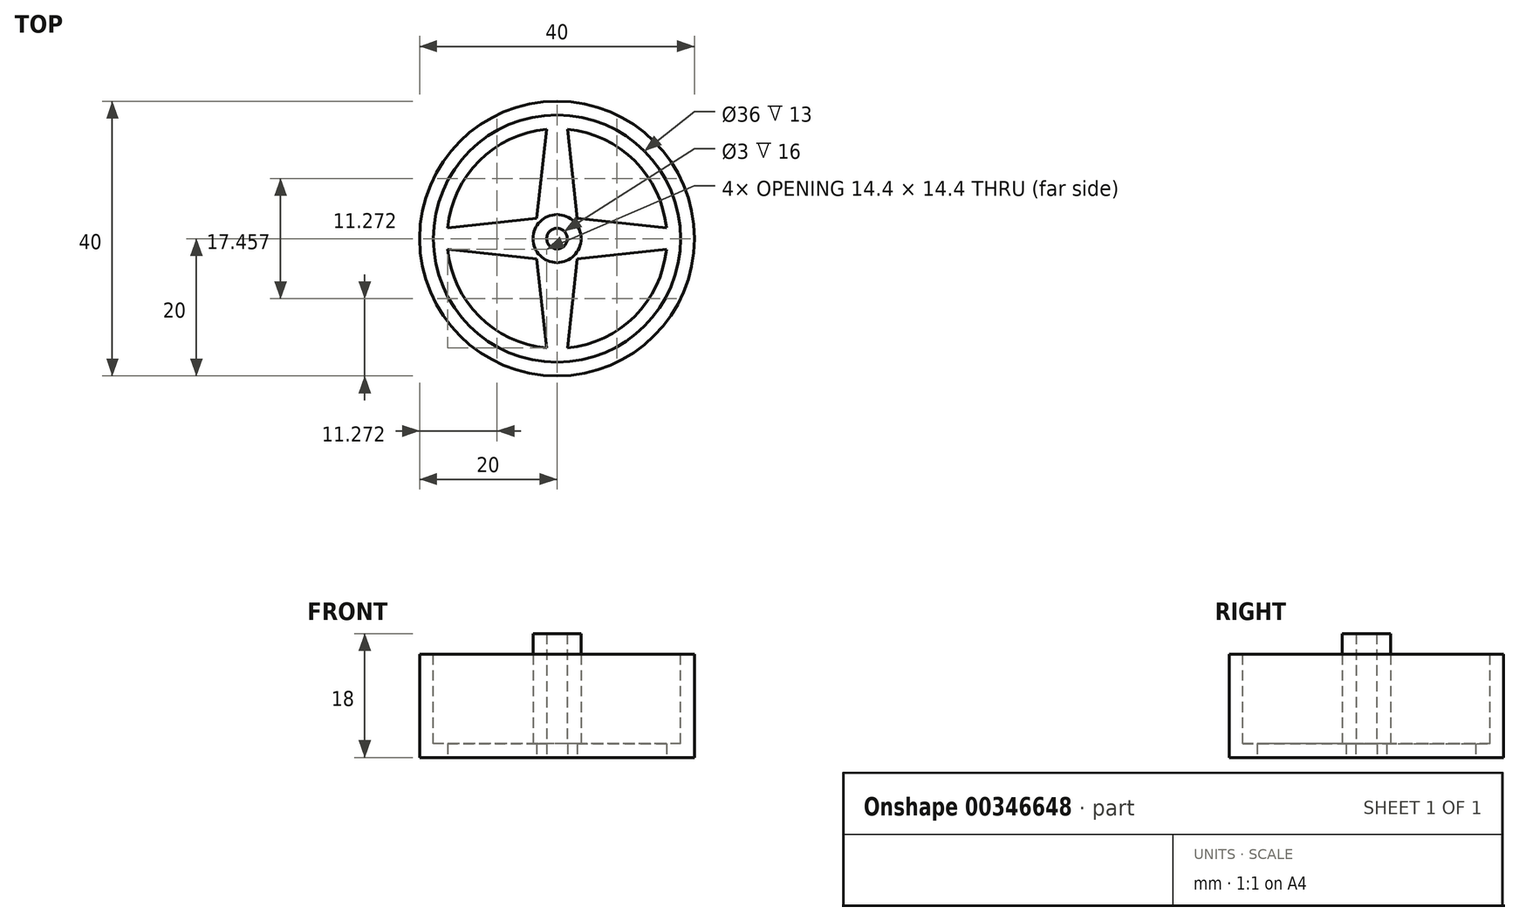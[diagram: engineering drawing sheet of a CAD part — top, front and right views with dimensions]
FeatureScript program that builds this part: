
annotation { "Feature Type Name" : "Feature", "Feature Type Description" : "" }
export const myFeature = defineFeature(function(context is Context, id is Id, definition is map)
    precondition{}
    {
        {
            var Q0;
            Q0=qCreatedBy(makeId("Top.planeOp"),FACE);
            var sketch = newSketch(context, id + "F0", { "sketchPlane" : qUnion([Q0])});
            skCircle(sketch, "E0", {"center": v(0, 0) * mm, "radius": 20 * mm});
            skSolve(sketch);
        }
        {
            var Q0;
            Q0=makeQuery(id+"F0.imprint","IMPRINT",FACE,{"disambiguationData":[TD([[makeQuery(id+"F0.imprint","IMPRINT",EDGE,{"derivedFrom":sQuery(id+"F0.wireOp",EDGE,"E0")}),1.0]])]});
            extrude(context, id + "F1", {"entities" : qUnion([Q0]), "depth" : 15 * mm});
        }
        {
            var Q0;
            Q0=makeQuery(id+"F1.opExtrude","CAP_FACE",FACE,{"disambiguationData":[OSD([sQuery(id+"F0.wireOp",EDGE,"E0")])],"isStart":false});
            var sketch = newSketch(context, id + "F2", { "sketchPlane" : qUnion([Q0])});
            skCircle(sketch, "E1", {"center": v(0, 0) * mm, "radius": 18 * mm});
            skSolve(sketch);
        }
        {
            var Q0;
            Q0=makeQuery(id+"F2.imprint","IMPRINT",FACE,{"disambiguationData":[TD([[makeQuery(id+"F2.imprint","IMPRINT",EDGE,{"derivedFrom":sQuery(id+"F2.wireOp",EDGE,"E1")}),1.0]])]});
            extrude(context, id + "F3", {"entities" : qUnion([Q0]), "operationType" : NewBodyOperationType.REMOVE, "oppositeDirection" : true, "depth" : 13 * mm});
        }
        {
            var Q0;
            Q0=makeQuery(id+"F3.boolean.opBoolean","COPY",FACE,{"derivedFrom":makeQuery(id+"F3.opExtrude","CAP_FACE",FACE,{"disambiguationData":[OSD([sQuery(id+"F2.wireOp",EDGE,"E1")])],"isStart":false})});
            var sketch = newSketch(context, id + "F4", { "sketchPlane" : qUnion([Q0])});
            skCircle(sketch, "E2", {"center": v(0, 0) * mm, "radius": 1.5 * mm});
            skCircle(sketch, "E3", {"center": v(0, 0) * mm, "radius": 3.5 * mm});
            skSolve(sketch);
        }
        {
            var Q0;
            Q0=makeQuery(id+"F4.imprint","IMPRINT",FACE,{"disambiguationData":[TD([[makeQuery(id+"F4.imprint","IMPRINT",EDGE,{"derivedFrom":sQuery(id+"F4.wireOp",EDGE,"E2")}),-1.0]])]});
            extrude(context, id + "F5", {"entities" : qUnion([Q0]), "operationType" : NewBodyOperationType.ADD, "depth" : 16 * mm});
        }
        {
            var Q0;
            Q0=makeQuery(id+"F1.opExtrude","CAP_FACE",FACE,{"disambiguationData":[OSD([sQuery(id+"F0.wireOp",EDGE,"E0")])],"isStart":true});
            var sketch = newSketch(context, id + "F6", { "sketchPlane" : qUnion([Q0])});
            skCircle(sketch, "E4", {"center": v(0, 0) * mm, "radius": 18 * mm});
            skCircle(sketch, "E5", {"center": v(0, 0) * mm, "radius": 3.5 * mm});
            skCircle(sketch, "E6", {"center": v(0, 0) * mm, "radius": 16 * mm});
            skPoint(sketch, "E7.orphan", {"position": v(0, 18) * mm});
            skLineSegment(sketch, "E8", {"start": v(-3.09, 1.65) * mm, "end": v(-1.53, 15.93) * mm});
            skLineSegment(sketch, "E9.MirrorCS", {"start": v(3.09, 1.65) * mm, "end": v(1.53, 15.93) * mm});
            skLineSegment(sketch, "E10.1.0", {"start": v(-1.65, 3.09) * mm, "end": v(-15.93, 1.53) * mm});
            skLineSegment(sketch, "E10.1.1", {"start": v(-1.65, -3.09) * mm, "end": v(-15.93, -1.53) * mm});
            skLineSegment(sketch, "E10.2.0", {"start": v(-3.09, -1.65) * mm, "end": v(-1.53, -15.93) * mm});
            skLineSegment(sketch, "E10.2.1", {"start": v(3.09, -1.65) * mm, "end": v(1.53, -15.93) * mm});
            skLineSegment(sketch, "E10.3.0", {"start": v(1.65, -3.09) * mm, "end": v(15.93, -1.53) * mm});
            skLineSegment(sketch, "E10.3.1", {"start": v(1.65, 3.09) * mm, "end": v(15.93, 1.53) * mm});
            skSolve(sketch);
        }
        {
            var Q0;
            {var subQ0=sQuery(id+"F6.wireOp",EDGE,"E8");var subQ1=sQuery(id+"F6.wireOp",EDGE,"E6");var subQ2=makeQuery(id+"F6.imprint","INTERSECT",VERTEX,{"derivedFrom":[subQ1,subQ0]});Q0=makeQuery(id+"F6.imprint","IMPRINT",FACE,{"disambiguationData":[TD([[makeQuery(id+"F6.imprint","IMPRINT",EDGE,{"disambiguationData":[TD([[subQ2,-1.0]])],"derivedFrom":subQ1}),1.0]])]});}
            var Q1;
            {var subQ0=sQuery(id+"F6.wireOp",EDGE,"E10.1.1");var subQ1=sQuery(id+"F6.wireOp",EDGE,"E6");var subQ2=makeQuery(id+"F6.imprint","INTERSECT",VERTEX,{"derivedFrom":[subQ1,subQ0]});Q1=makeQuery(id+"F6.imprint","IMPRINT",FACE,{"disambiguationData":[TD([[makeQuery(id+"F6.imprint","IMPRINT",EDGE,{"disambiguationData":[TD([[subQ2,-1.0]])],"derivedFrom":subQ1}),1.0]])]});}
            var Q2;
            {var subQ0=sQuery(id+"F6.wireOp",EDGE,"E10.2.1");var subQ1=sQuery(id+"F6.wireOp",EDGE,"E6");var subQ2=makeQuery(id+"F6.imprint","INTERSECT",VERTEX,{"derivedFrom":[subQ1,subQ0]});Q2=makeQuery(id+"F6.imprint","IMPRINT",FACE,{"disambiguationData":[TD([[makeQuery(id+"F6.imprint","IMPRINT",EDGE,{"disambiguationData":[TD([[subQ2,-1.0]])],"derivedFrom":subQ1}),1.0]])]});}
            var Q3;
            {var subQ0=sQuery(id+"F6.wireOp",EDGE,"E9.MirrorCS");var subQ1=sQuery(id+"F6.wireOp",EDGE,"E6");var subQ2=makeQuery(id+"F6.imprint","INTERSECT",VERTEX,{"derivedFrom":[subQ1,subQ0]});Q3=makeQuery(id+"F6.imprint","IMPRINT",FACE,{"disambiguationData":[TD([[makeQuery(id+"F6.imprint","IMPRINT",EDGE,{"disambiguationData":[TD([[subQ2,1.0]])],"derivedFrom":subQ1}),1.0]])]});}
            extrude(context, id + "F7", {"entities" : qUnion([Q0, Q1, Q2, Q3]), "operationType" : NewBodyOperationType.REMOVE, "oppositeDirection" : true, "depth" : 2 * mm});
        }
    });
